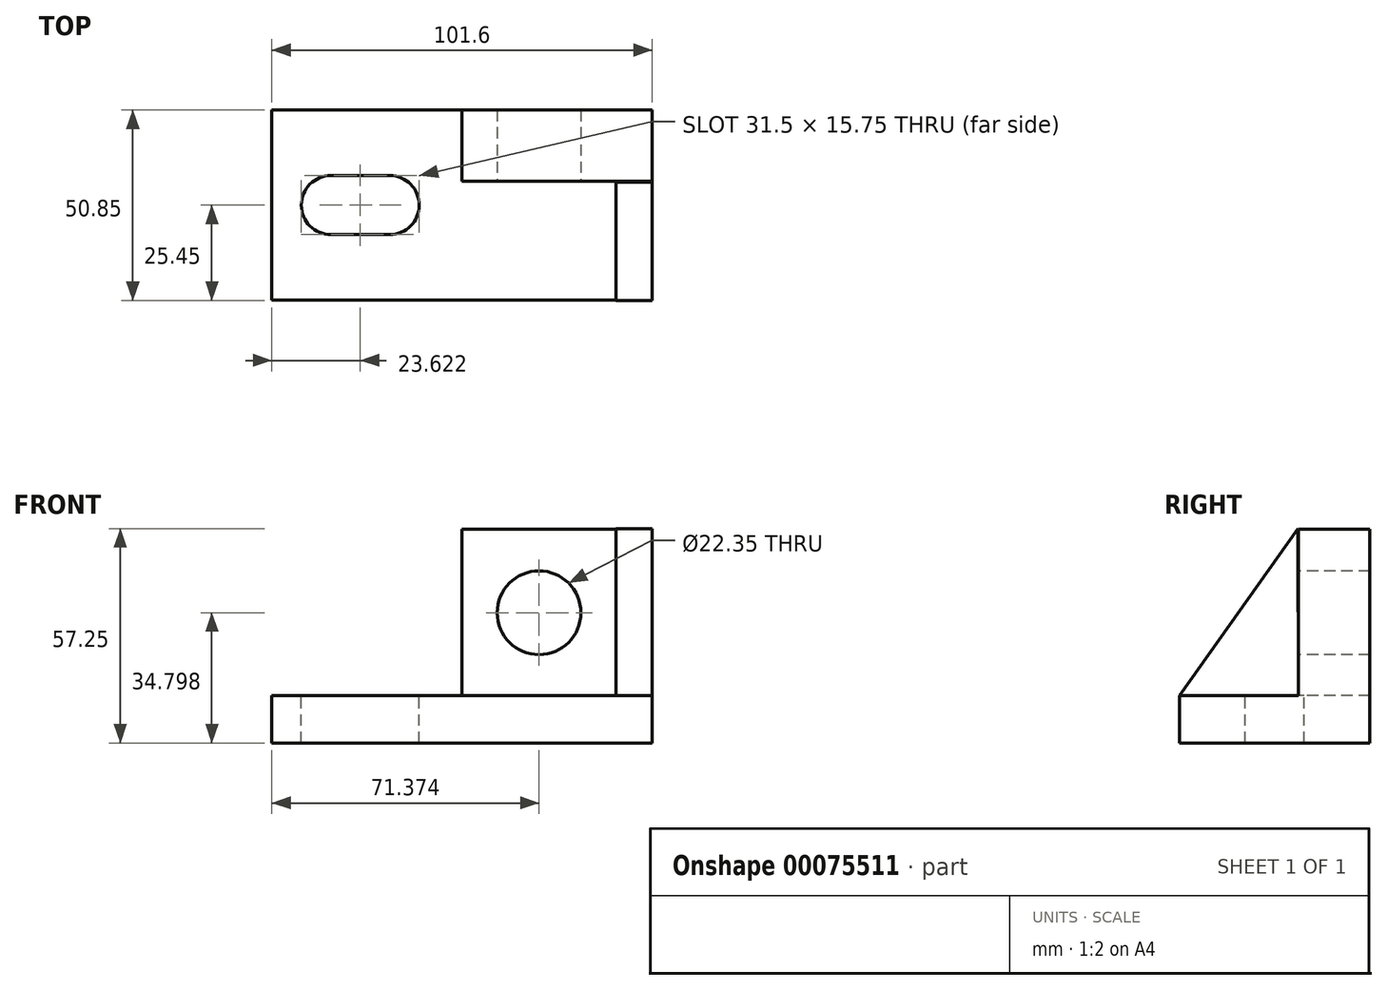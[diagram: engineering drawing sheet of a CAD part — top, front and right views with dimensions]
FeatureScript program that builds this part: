
annotation { "Feature Type Name" : "Feature", "Feature Type Description" : "" }
export const myFeature = defineFeature(function(context is Context, id is Id, definition is map)
    precondition{}
    {
        {
            var Q0;
            Q0=qCreatedBy(makeId("Top.planeOp"),FACE);
            var sketch = newSketch(context, id + "F0", { "sketchPlane" : qUnion([Q0])});
            skLineSegment(sketch, "E0.rect.bottom", {"start": v(-50.8, 25.4) * mm, "end": v(50.8, 25.4) * mm});
            skLineSegment(sketch, "E0.rect.top", {"start": v(-50.8, -25.4) * mm, "end": v(50.8, -25.4) * mm});
            skLineSegment(sketch, "E0.rect.left", {"start": v(-50.8, 25.4) * mm, "end": v(-50.8, -25.4) * mm});
            skLineSegment(sketch, "E0.rect.right", {"start": v(50.8, 25.4) * mm, "end": v(50.8, -25.4) * mm});
            skPoint(sketch, "E0.rect.middle", {"position": v(0, 0) * mm});
            skSolve(sketch);
        }
        {
            var Q0;
            Q0 = qSketchRegion(id + "F0", true);
            extrude(context, id + "F1", {"entities" : qUnion([Q0]), "depth" : 12.7 * mm});
        }
        {
            var Q0;
            Q0=makeQuery(id+"F1.opExtrude","CAP_FACE",FACE,{"disambiguationData":[OSD([sQuery(id+"F0.wireOp",EDGE,"E0.rect.bottom"),sQuery(id+"F0.wireOp",EDGE,"E0.rect.top"),sQuery(id+"F0.wireOp",EDGE,"E0.rect.left"),sQuery(id+"F0.wireOp",EDGE,"E0.rect.right")])],"isStart":false});
            var sketch = newSketch(context, id + "F2", { "sketchPlane" : qUnion([Q0])});
            skLineSegment(sketch, "E1.bottom", {"start": v(50.8, 25.4) * mm, "end": v(0, 25.4) * mm});
            skLineSegment(sketch, "E1.top", {"start": v(50.8, 6.35) * mm, "end": v(0, 6.35) * mm});
            skLineSegment(sketch, "E1.left", {"start": v(50.8, 25.4) * mm, "end": v(50.8, 6.35) * mm});
            skLineSegment(sketch, "E1.right", {"start": v(0, 25.4) * mm, "end": v(0, 6.35) * mm});
            skSolve(sketch);
        }
        {
            var Q0;
            Q0 = qSketchRegion(id + "F2", true);
            extrude(context, id + "F3", {"entities" : qUnion([Q0]), "operationType" : NewBodyOperationType.ADD, "depth" : 44.45 * mm});
        }
        {
            var Q0;
            Q0=makeQuery(id+"F3.opExtrude","SWEPT_FACE",FACE,{"disambiguationData":[OSD([sQuery(id+"F2.wireOp",EDGE,"E1.top")])]});
            var sketch = newSketch(context, id + "F4", { "sketchPlane" : qUnion([Q0])});
            skPoint(sketch, "E2", {"position": v(20.57, 34.8) * mm});
            skSolve(sketch);
        }
        {
            var Q0;
            Q0=sQuery(id+"F4.wireOp",VERTEX,"E2");
            var Q1;
            Q1=makeQuery(id+"F1.opExtrude","SWEPT_BODY",BODY,{"disambiguationData":[OSD([sQuery(id+"F0.wireOp",EDGE,"E0.rect.bottom"),sQuery(id+"F0.wireOp",EDGE,"E0.rect.top"),sQuery(id+"F0.wireOp",EDGE,"E0.rect.left"),sQuery(id+"F0.wireOp",EDGE,"E0.rect.right")])]});
            hole(context, id + "F5", {"style" : HoleStyle.SIMPLE, "holeDiameter" : 22.35 * mm, "endStyle" : HoleEndStyle.THROUGH, "locations" : qUnion([Q0]), "scope" : qUnion([Q1])});
        }
        {
            var Q0;
            Q0=makeQuery(id+"F3.boolean.opBoolean","MERGE",FACE,{"derivedFrom":[makeQuery(id+"F1.opExtrude","SWEPT_FACE",FACE,{"disambiguationData":[OSD([sQuery(id+"F0.wireOp",EDGE,"E0.rect.right")])]}),makeQuery(id+"F3.opExtrude","SWEPT_FACE",FACE,{"disambiguationData":[OSD([sQuery(id+"F2.wireOp",EDGE,"E1.left")])]})]});
            var sketch = newSketch(context, id + "F6", { "sketchPlane" : qUnion([Q0])});
            skLineSegment(sketch, "E3", {"start": v(6.12, 57.25) * mm, "end": v(-25.45, 12.7) * mm});
            skLineSegment(sketch, "E4", {"start": v(-25.45, 12.7) * mm, "end": v(6.34, 12.7) * mm});
            skLineSegment(sketch, "E5", {"start": v(6.34, 12.7) * mm, "end": v(6.12, 57.25) * mm});
            skSolve(sketch);
        }
        {
            var Q0;
            Q0 = qSketchRegion(id + "F6", true);
            extrude(context, id + "F7", {"entities" : qUnion([Q0]), "oppositeDirection" : true, "depth" : 9.65 * mm});
        }
        {
            var Q0;
            Q0=makeQuery(id+"F1.opExtrude","CAP_FACE",FACE,{"disambiguationData":[OSD([sQuery(id+"F0.wireOp",EDGE,"E0.rect.bottom"),sQuery(id+"F0.wireOp",EDGE,"E0.rect.top"),sQuery(id+"F0.wireOp",EDGE,"E0.rect.left"),sQuery(id+"F0.wireOp",EDGE,"E0.rect.right")])],"isStart":false});
            var sketch = newSketch(context, id + "F8", { "sketchPlane" : qUnion([Q0])});
            skLineSegment(sketch, "E6.bottom", {"start": v(-35.05, 7.87) * mm, "end": v(-19.3, 7.87) * mm});
            skLineSegment(sketch, "E6.top", {"start": v(-35.05, -7.87) * mm, "end": v(-19.3, -7.87) * mm});
            skArc(sketch, "E7", {"start": v(-19.3, -7.87) * mm, "mid": v(-11.43, 0) * mm, "end": v(-19.3, 7.87) * mm});
            skArc(sketch, "E8", {"start": v(-35.05, 7.87) * mm, "mid": v(-42.93, 0) * mm, "end": v(-35.05, -7.87) * mm});
            skSolve(sketch);
        }
        {
            var Q0;
            Q0 = qSketchRegion(id + "F8", true);
            extrude(context, id + "F9", {"entities" : qUnion([Q0]), "operationType" : NewBodyOperationType.REMOVE, "oppositeDirection" : true, "depth" : 25.4 * mm});
        }
    });
